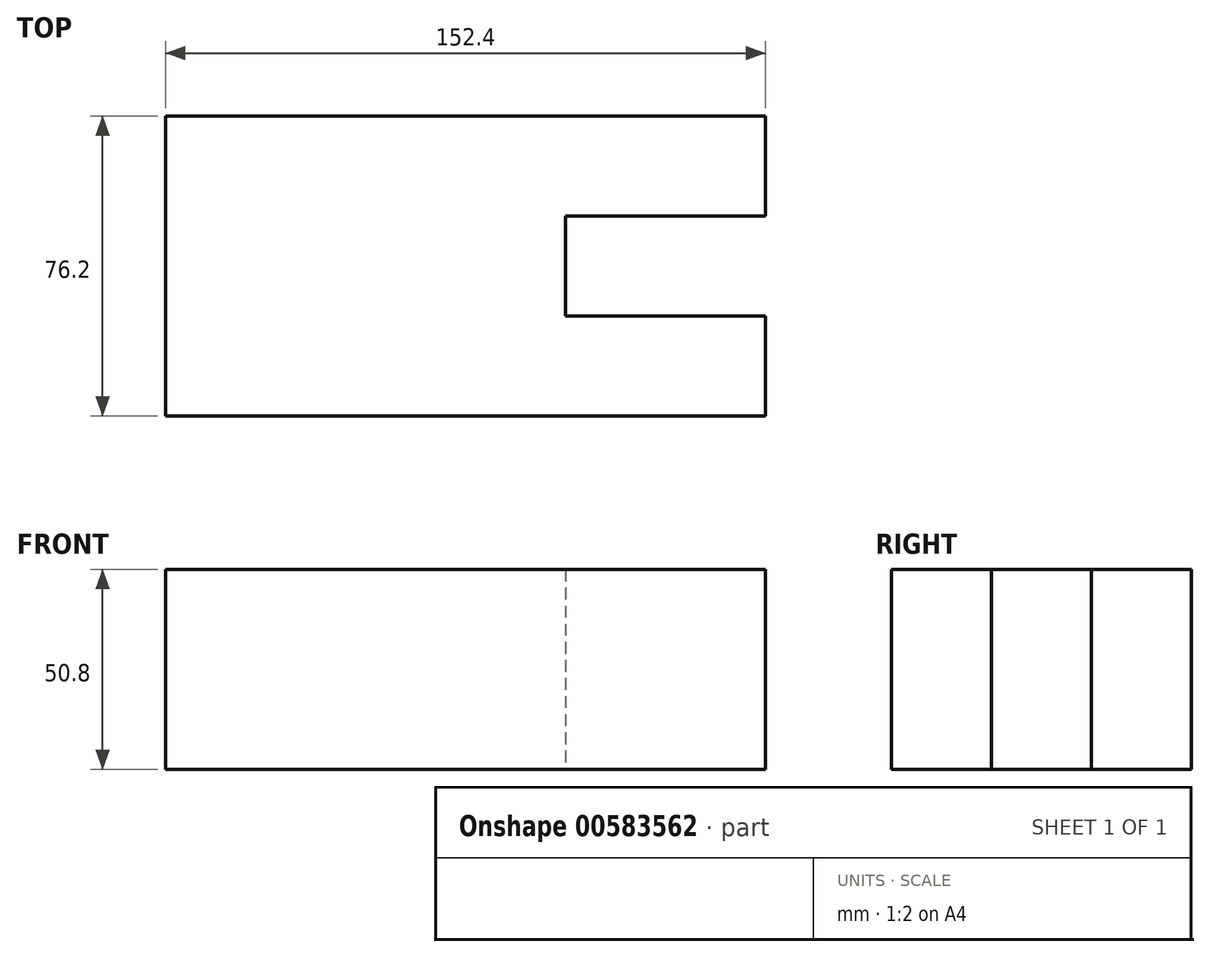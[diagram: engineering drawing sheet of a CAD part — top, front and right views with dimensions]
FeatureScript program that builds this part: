
annotation { "Feature Type Name" : "Feature", "Feature Type Description" : "" }
export const myFeature = defineFeature(function(context is Context, id is Id, definition is map)
    precondition{}
    {
        {
            var Q0;
            Q0=qCreatedBy(makeId("Top.planeOp"),FACE);
            var sketch = newSketch(context, id + "F0", { "sketchPlane" : qUnion([Q0])});
            skLineSegment(sketch, "E0", {"start": v(0, 0) * mm, "end": v(0, -76.2) * mm});
            skLineSegment(sketch, "E1", {"start": v(0, 0) * mm, "end": v(152.4, 0) * mm});
            skLineSegment(sketch, "E2", {"start": v(0, -76.2) * mm, "end": v(152.4, -76.2) * mm});
            skLineSegment(sketch, "E3", {"start": v(152.4, -76.2) * mm, "end": v(152.4, -50.8) * mm});
            skLineSegment(sketch, "E4", {"start": v(152.4, -50.8) * mm, "end": v(101.6, -50.8) * mm});
            skLineSegment(sketch, "E5", {"start": v(101.6, -50.8) * mm, "end": v(101.6, -25.4) * mm});
            skLineSegment(sketch, "E6", {"start": v(101.6, -25.4) * mm, "end": v(152.4, -25.4) * mm});
            skLineSegment(sketch, "E7", {"start": v(152.4, -25.4) * mm, "end": v(152.4, 0) * mm});
            skSolve(sketch);
        }
        {
            var Q0;
            Q0 = qSketchRegion(id + "F0", true);
            extrude(context, id + "F1", {"entities" : qUnion([Q0]), "depth" : 50.8 * mm, "offsetDistance" : 25.4 * mm});
        }
    });
